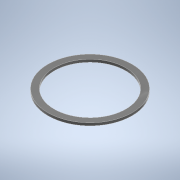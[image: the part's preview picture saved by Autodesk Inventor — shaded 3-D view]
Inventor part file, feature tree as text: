
AUTODESK INVENTOR PART (.ipt)
format: ipt  version: 2021 (Build 250183000, 183)  size: 101,888 bytes
history: native  units: mm
features: extrude x1, sketch x1
ambient origin geometry x8: Origin, YZ Plane, XZ Plane, XY Plane, X Axis, Y Axis, Z Axis, Center Point
bodies: Solid1 (feature_tree)
feature tree (2):
  extrude  "Extrusion1"  Depth=0.3mm
  sketch  "Sketch1"  dims[d0=9.5mm d1=8.1mm d2=0.3mm d3=0.0mm]
